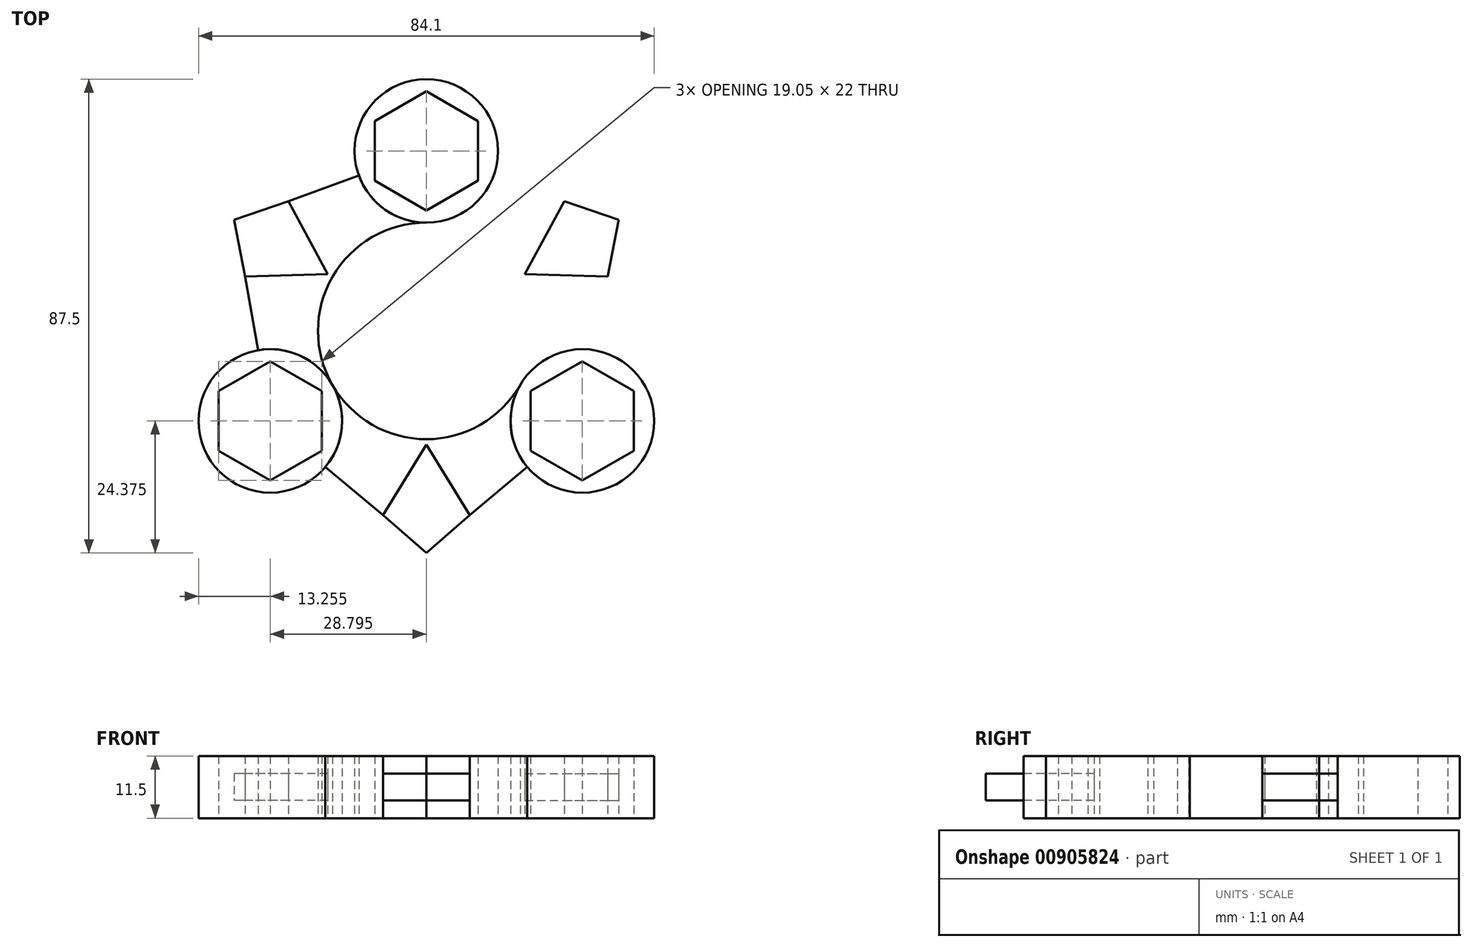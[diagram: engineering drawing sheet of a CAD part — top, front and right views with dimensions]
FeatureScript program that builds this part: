
annotation { "Feature Type Name" : "Feature", "Feature Type Description" : "" }
export const myFeature = defineFeature(function(context is Context, id is Id, definition is map)
    precondition{}
    {
        {
            var Q0;
            Q0=qCreatedBy(makeId("Top.planeOp"),FACE);
            var sketch = newSketch(context, id + "F0", { "sketchPlane" : qUnion([Q0])});
            skCircle(sketch, "E0", {"center": v(0, 0) * mm, "radius": 20 * mm});
            skLineSegment(sketch, "E1", {"start": v(0, 22.25) * mm, "end": v(0, 44.25) * mm});
            skCircle(sketch, "E2", {"center": v(0, 33.25) * mm, "radius": 11 * mm});
            skLineSegment(sketch, "E3", {"start": v(0, 44.25) * mm, "end": v(9.53, 38.75) * mm});
            skLineSegment(sketch, "E4", {"start": v(9.53, 38.75) * mm, "end": v(9.53, 27.75) * mm});
            skLineSegment(sketch, "E5", {"start": v(9.53, 27.75) * mm, "end": v(0, 22.25) * mm});
            skLineSegment(sketch, "E6", {"start": v(0, 22.25) * mm, "end": v(-9.53, 27.75) * mm});
            skLineSegment(sketch, "E7", {"start": v(-9.53, 27.75) * mm, "end": v(-9.53, 38.75) * mm});
            skLineSegment(sketch, "E8", {"start": v(-9.53, 38.75) * mm, "end": v(0, 44.25) * mm});
            skCircle(sketch, "E9", {"center": v(0, 33.25) * mm, "radius": 13.25 * mm});
            skLineSegment(sketch, "E10.1.0", {"start": v(-19.27, -22.12) * mm, "end": v(-28.8, -27.62) * mm});
            skLineSegment(sketch, "E10.1.1", {"start": v(-28.8, -27.62) * mm, "end": v(-38.32, -22.12) * mm});
            skLineSegment(sketch, "E10.1.2", {"start": v(-38.32, -22.12) * mm, "end": v(-38.32, -11.13) * mm});
            skLineSegment(sketch, "E10.1.3", {"start": v(-38.32, -11.13) * mm, "end": v(-28.8, -5.62) * mm});
            skLineSegment(sketch, "E10.1.4", {"start": v(-28.8, -5.63) * mm, "end": v(-19.27, -11.13) * mm});
            skLineSegment(sketch, "E10.1.5", {"start": v(-19.27, -11.12) * mm, "end": v(-19.27, -22.12) * mm});
            skCircle(sketch, "E10.1.6", {"center": v(-28.8, -16.62) * mm, "radius": 11 * mm});
            skCircle(sketch, "E10.1.7", {"center": v(-28.8, -16.62) * mm, "radius": 13.25 * mm});
            skLineSegment(sketch, "E10.2.0", {"start": v(28.8, -5.63) * mm, "end": v(38.32, -11.13) * mm});
            skLineSegment(sketch, "E10.2.1", {"start": v(38.32, -11.13) * mm, "end": v(38.32, -22.13) * mm});
            skLineSegment(sketch, "E10.2.2", {"start": v(38.32, -22.13) * mm, "end": v(28.8, -27.63) * mm});
            skLineSegment(sketch, "E10.2.3", {"start": v(28.8, -27.63) * mm, "end": v(19.27, -22.13) * mm});
            skLineSegment(sketch, "E10.2.4", {"start": v(19.27, -22.13) * mm, "end": v(19.27, -11.13) * mm});
            skLineSegment(sketch, "E10.2.5", {"start": v(19.27, -11.13) * mm, "end": v(28.8, -5.63) * mm});
            skCircle(sketch, "E10.2.6", {"center": v(28.8, -16.63) * mm, "radius": 11 * mm});
            skCircle(sketch, "E10.2.7", {"center": v(28.8, -16.63) * mm, "radius": 13.25 * mm});
            skLineSegment(sketch, "E11", {"start": v(0, 0) * mm, "end": v(17.32, 10) * mm});
            skLineSegment(sketch, "E12", {"start": v(17.32, 10) * mm, "end": v(35.5, 20.5) * mm});
            skLineSegment(sketch, "E13", {"start": v(35.5, 20.5) * mm, "end": v(18.19, 10.5) * mm});
            skLineSegment(sketch, "E14", {"start": v(18.19, 10.5) * mm, "end": v(33.44, 10.07) * mm});
            skLineSegment(sketch, "E15", {"start": v(33.44, 10.07) * mm, "end": v(35.5, 20.5) * mm});
            skLineSegment(sketch, "E16", {"start": v(33.44, 10.07) * mm, "end": v(29.44, 17) * mm});
            skLineSegment(sketch, "E17.MirrorCS", {"start": v(18.19, 10.5) * mm, "end": v(25.44, 23.93) * mm});
            skLineSegment(sketch, "E18.MirrorCS", {"start": v(25.44, 23.93) * mm, "end": v(35.5, 20.5) * mm});
            skLineSegment(sketch, "E19", {"start": v(0, 33.25) * mm, "end": v(25.44, 23.93) * mm});
            skLineSegment(sketch, "E20", {"start": v(33.44, 10.07) * mm, "end": v(28.8, -16.62) * mm});
            skLineSegment(sketch, "E21.1.0", {"start": v(-28.8, -16.63) * mm, "end": v(-33.44, 10.07) * mm});
            skLineSegment(sketch, "E21.1.1", {"start": v(-33.44, 10.07) * mm, "end": v(-35.5, 20.5) * mm});
            skLineSegment(sketch, "E21.1.2", {"start": v(-18.19, 10.5) * mm, "end": v(-33.44, 10.07) * mm});
            skLineSegment(sketch, "E21.1.3", {"start": v(-18.19, 10.5) * mm, "end": v(-25.44, 23.93) * mm});
            skLineSegment(sketch, "E21.1.4", {"start": v(-25.44, 23.93) * mm, "end": v(-35.5, 20.5) * mm});
            skLineSegment(sketch, "E21.1.5", {"start": v(-25.44, 23.93) * mm, "end": v(0, 33.25) * mm});
            skLineSegment(sketch, "E21.2.0", {"start": v(28.8, -16.63) * mm, "end": v(8, -34) * mm});
            skLineSegment(sketch, "E21.2.1", {"start": v(8, -34) * mm, "end": v(0, -41) * mm});
            skLineSegment(sketch, "E21.2.2", {"start": v(0, -21) * mm, "end": v(8, -34) * mm});
            skLineSegment(sketch, "E21.2.3", {"start": v(0, -21) * mm, "end": v(-8, -34) * mm});
            skLineSegment(sketch, "E21.2.4", {"start": v(-8, -34) * mm, "end": v(0, -41) * mm});
            skLineSegment(sketch, "E21.2.5", {"start": v(-8, -34) * mm, "end": v(-28.8, -16.62) * mm});
            skSolve(sketch);
        }
        {
            var Q0;
            {var subQ1=sQuery(id+"F0.wireOp",EDGE,"E12");Q0=makeQuery(id+"F0.imprint","IMPRINT",FACE,{"disambiguationData":[TD([[makeQuery(id+"F0.imprint","IMPRINT",EDGE,{"derivedFrom":subQ1}),1.0]])]});}
            var Q1;
            {var subQ6=sQuery(id+"F0.wireOp",EDGE,"E12");Q1=makeQuery(id+"F0.imprint","IMPRINT",FACE,{"disambiguationData":[TD([[makeQuery(id+"F0.imprint","IMPRINT",EDGE,{"derivedFrom":subQ6}),-1.0]])]});}
            var Q2;
            {var subQ0=sQuery(id+"F0.wireOp",EDGE,"E21.2.2");Q2=makeQuery(id+"F0.imprint","IMPRINT",FACE,{"disambiguationData":[TD([[makeQuery(id+"F0.imprint","IMPRINT",EDGE,{"derivedFrom":subQ0}),1.0]])]});}
            var Q3;
            {var subQ0=sQuery(id+"F0.wireOp",EDGE,"E21.1.2");Q3=makeQuery(id+"F0.imprint","IMPRINT",FACE,{"disambiguationData":[TD([[makeQuery(id+"F0.imprint","IMPRINT",EDGE,{"derivedFrom":subQ0}),1.0]])]});}
            extrude(context, id + "F1", {"entities" : qUnion([Q0, Q1, Q2, Q3]), "endBound" : BoundingType.SYMMETRIC, "depth" : 11.5 * mm, "offsetDistance" : 25 * mm});
        }
        {
            var Q0;
            {var subQ3=sQuery(id+"F0.wireOp",EDGE,"E17.MirrorCS");Q0=makeQuery(id+"F0.imprint","IMPRINT",FACE,{"disambiguationData":[TD([[makeQuery(id+"F0.imprint","IMPRINT",EDGE,{"derivedFrom":subQ3}),-1.0]])]});}
            var Q1;
            {var subQ0=sQuery(id+"F0.wireOp",EDGE,"E15");Q1=makeQuery(id+"F0.imprint","IMPRINT",FACE,{"disambiguationData":[TD([[makeQuery(id+"F0.imprint","IMPRINT",EDGE,{"derivedFrom":subQ0}),1.0]])]});}
            var Q2;
            {var subQ0=sQuery(id+"F0.wireOp",EDGE,"E14");Q2=makeQuery(id+"F0.imprint","IMPRINT",FACE,{"disambiguationData":[TD([[makeQuery(id+"F0.imprint","IMPRINT",EDGE,{"derivedFrom":subQ0}),1.0]])]});}
            var Q3;
            Q3=makeQuery(id+"F0.imprint","IMPRINT",FACE,{"disambiguationData":[TD([[makeQuery(id+"F0.imprint","IMPRINT",EDGE,{"derivedFrom":sQuery(id+"F0.wireOp",EDGE,"E21.1.1")}),-1.0]])]});
            var Q4;
            Q4=makeQuery(id+"F0.imprint","IMPRINT",FACE,{"disambiguationData":[TD([[makeQuery(id+"F0.imprint","IMPRINT",EDGE,{"derivedFrom":sQuery(id+"F0.wireOp",EDGE,"E21.2.1")}),-1.0]])]});
            extrude(context, id + "F2", {"entities" : qUnion([Q0, Q1, Q2, Q3, Q4]), "endBound" : BoundingType.SYMMETRIC, "depth" : 5 * mm, "offsetDistance" : 25 * mm});
        }
        {
            var Q0;
            {var subQ7=sQuery(id+"F0.wireOp",EDGE,"E20");var subQ9=sQuery(id+"F0.wireOp",EDGE,"E10.2.7");var subQ10=makeQuery(id+"F0.imprint","INTERSECT",VERTEX,{"derivedFrom":[subQ9,subQ7]});Q0=makeQuery(id+"F0.imprint","IMPRINT",FACE,{"disambiguationData":[TD([[makeQuery(id+"F0.imprint","IMPRINT",EDGE,{"disambiguationData":[TD([[subQ10,1.0]])],"derivedFrom":subQ9}),1.0]])]});}
            var Q1;
            {var subQ1=sQuery(id+"F0.wireOp",EDGE,"E10.2.0");var subQ3=sQuery(id+"F0.wireOp",EDGE,"E20");var subQ4=makeQuery(id+"F0.imprint","INTERSECT",VERTEX,{"derivedFrom":[subQ1,subQ3]});Q1=makeQuery(id+"F0.imprint","IMPRINT",FACE,{"disambiguationData":[TD([[makeQuery(id+"F0.imprint","IMPRINT",EDGE,{"disambiguationData":[TD([[subQ4,1.0]])],"derivedFrom":subQ3}),1.0]])]});}
            var Q2;
            {var subQ0=sQuery(id+"F0.wireOp",EDGE,"E10.2.1");Q2=makeQuery(id+"F0.imprint","IMPRINT",FACE,{"disambiguationData":[TD([[makeQuery(id+"F0.imprint","IMPRINT",EDGE,{"derivedFrom":subQ0}),1.0]])]});}
            var Q3;
            {var subQ0=sQuery(id+"F0.wireOp",EDGE,"E10.2.2");Q3=makeQuery(id+"F0.imprint","IMPRINT",FACE,{"disambiguationData":[TD([[makeQuery(id+"F0.imprint","IMPRINT",EDGE,{"derivedFrom":subQ0}),1.0]])]});}
            var Q4;
            {var subQ1=sQuery(id+"F0.wireOp",EDGE,"E10.2.3");var subQ3=sQuery(id+"F0.wireOp",EDGE,"E21.2.0");var subQ4=makeQuery(id+"F0.imprint","INTERSECT",VERTEX,{"derivedFrom":[subQ1,subQ3]});Q4=makeQuery(id+"F0.imprint","IMPRINT",FACE,{"disambiguationData":[TD([[makeQuery(id+"F0.imprint","IMPRINT",EDGE,{"disambiguationData":[TD([[subQ4,-1.0]])],"derivedFrom":subQ3}),1.0]])]});}
            var Q5;
            {var subQ0=sQuery(id+"F0.wireOp",EDGE,"E10.2.4");Q5=makeQuery(id+"F0.imprint","IMPRINT",FACE,{"disambiguationData":[TD([[makeQuery(id+"F0.imprint","IMPRINT",EDGE,{"derivedFrom":subQ0}),1.0]])]});}
            var Q6;
            {var subQ0=sQuery(id+"F0.wireOp",EDGE,"E10.2.5");Q6=makeQuery(id+"F0.imprint","IMPRINT",FACE,{"disambiguationData":[TD([[makeQuery(id+"F0.imprint","IMPRINT",EDGE,{"derivedFrom":subQ0}),1.0]])]});}
            var Q7;
            {var subQ1=sQuery(id+"F0.wireOp",EDGE,"E10.2.0");var subQ3=sQuery(id+"F0.wireOp",EDGE,"E20");var subQ4=makeQuery(id+"F0.imprint","INTERSECT",VERTEX,{"derivedFrom":[subQ1,subQ3]});Q7=makeQuery(id+"F0.imprint","IMPRINT",FACE,{"disambiguationData":[TD([[makeQuery(id+"F0.imprint","IMPRINT",EDGE,{"disambiguationData":[TD([[subQ4,1.0]])],"derivedFrom":subQ3}),-1.0]])]});}
            var Q8;
            {var subQ8=sQuery(id+"F0.wireOp",EDGE,"E20");var subQ10=sQuery(id+"F0.wireOp",EDGE,"E10.2.7");var subQ11=makeQuery(id+"F0.imprint","INTERSECT",VERTEX,{"derivedFrom":[subQ10,subQ8]});Q8=makeQuery(id+"F0.imprint","IMPRINT",FACE,{"disambiguationData":[TD([[makeQuery(id+"F0.imprint","IMPRINT",EDGE,{"disambiguationData":[TD([[subQ11,-1.0]])],"derivedFrom":subQ10}),1.0]])]});}
            var Q9;
            {var subQ1=sQuery(id+"F0.wireOp",EDGE,"E10.2.3");var subQ3=sQuery(id+"F0.wireOp",EDGE,"E21.2.0");var subQ4=makeQuery(id+"F0.imprint","INTERSECT",VERTEX,{"derivedFrom":[subQ1,subQ3]});Q9=makeQuery(id+"F0.imprint","IMPRINT",FACE,{"disambiguationData":[TD([[makeQuery(id+"F0.imprint","IMPRINT",EDGE,{"disambiguationData":[TD([[subQ4,-1.0]])],"derivedFrom":subQ3}),-1.0]])]});}
            var Q10;
            {var subQ0=sQuery(id+"F0.wireOp",EDGE,"E10.1.5");Q10=makeQuery(id+"F0.imprint","IMPRINT",FACE,{"disambiguationData":[TD([[makeQuery(id+"F0.imprint","IMPRINT",EDGE,{"derivedFrom":subQ0}),1.0]])]});}
            var Q11;
            {var subQ8=sQuery(id+"F0.wireOp",EDGE,"E10.1.7");var subQ10=sQuery(id+"F0.wireOp",EDGE,"E21.2.5");var subQ12=makeQuery(id+"F0.imprint","INTERSECT",VERTEX,{"derivedFrom":[subQ8,subQ10]});Q11=makeQuery(id+"F0.imprint","IMPRINT",FACE,{"disambiguationData":[TD([[makeQuery(id+"F0.imprint","IMPRINT",EDGE,{"disambiguationData":[TD([[subQ12,-1.0]])],"derivedFrom":subQ8}),1.0]])]});}
            var Q12;
            {var subQ1=sQuery(id+"F0.wireOp",EDGE,"E10.1.0");var subQ3=sQuery(id+"F0.wireOp",EDGE,"E21.2.5");var subQ4=makeQuery(id+"F0.imprint","INTERSECT",VERTEX,{"derivedFrom":[subQ1,subQ3]});Q12=makeQuery(id+"F0.imprint","IMPRINT",FACE,{"disambiguationData":[TD([[makeQuery(id+"F0.imprint","IMPRINT",EDGE,{"disambiguationData":[TD([[subQ4,1.0]])],"derivedFrom":subQ3}),-1.0]])]});}
            var Q13;
            {var subQ7=sQuery(id+"F0.wireOp",EDGE,"E21.2.5");var subQ10=sQuery(id+"F0.wireOp",EDGE,"E10.1.7");var subQ11=makeQuery(id+"F0.imprint","INTERSECT",VERTEX,{"derivedFrom":[subQ10,subQ7]});Q13=makeQuery(id+"F0.imprint","IMPRINT",FACE,{"disambiguationData":[TD([[makeQuery(id+"F0.imprint","IMPRINT",EDGE,{"disambiguationData":[TD([[subQ11,1.0]])],"derivedFrom":subQ10}),1.0]])]});}
            var Q14;
            {var subQ1=sQuery(id+"F0.wireOp",EDGE,"E10.1.0");var subQ3=sQuery(id+"F0.wireOp",EDGE,"E21.2.5");var subQ4=makeQuery(id+"F0.imprint","INTERSECT",VERTEX,{"derivedFrom":[subQ1,subQ3]});Q14=makeQuery(id+"F0.imprint","IMPRINT",FACE,{"disambiguationData":[TD([[makeQuery(id+"F0.imprint","IMPRINT",EDGE,{"disambiguationData":[TD([[subQ4,1.0]])],"derivedFrom":subQ3}),1.0]])]});}
            var Q15;
            {var subQ0=sQuery(id+"F0.wireOp",EDGE,"E10.1.1");Q15=makeQuery(id+"F0.imprint","IMPRINT",FACE,{"disambiguationData":[TD([[makeQuery(id+"F0.imprint","IMPRINT",EDGE,{"derivedFrom":subQ0}),1.0]])]});}
            var Q16;
            {var subQ0=sQuery(id+"F0.wireOp",EDGE,"E10.1.2");Q16=makeQuery(id+"F0.imprint","IMPRINT",FACE,{"disambiguationData":[TD([[makeQuery(id+"F0.imprint","IMPRINT",EDGE,{"derivedFrom":subQ0}),1.0]])]});}
            var Q17;
            {var subQ1=sQuery(id+"F0.wireOp",EDGE,"E10.1.3");var subQ3=sQuery(id+"F0.wireOp",EDGE,"E21.1.0");var subQ4=makeQuery(id+"F0.imprint","INTERSECT",VERTEX,{"derivedFrom":[subQ1,subQ3]});Q17=makeQuery(id+"F0.imprint","IMPRINT",FACE,{"disambiguationData":[TD([[makeQuery(id+"F0.imprint","IMPRINT",EDGE,{"disambiguationData":[TD([[subQ4,-1.0]])],"derivedFrom":subQ3}),1.0]])]});}
            var Q18;
            {var subQ1=sQuery(id+"F0.wireOp",EDGE,"E10.1.3");var subQ3=sQuery(id+"F0.wireOp",EDGE,"E21.1.0");var subQ4=makeQuery(id+"F0.imprint","INTERSECT",VERTEX,{"derivedFrom":[subQ1,subQ3]});Q18=makeQuery(id+"F0.imprint","IMPRINT",FACE,{"disambiguationData":[TD([[makeQuery(id+"F0.imprint","IMPRINT",EDGE,{"disambiguationData":[TD([[subQ4,-1.0]])],"derivedFrom":subQ3}),-1.0]])]});}
            var Q19;
            {var subQ0=sQuery(id+"F0.wireOp",EDGE,"E10.1.4");Q19=makeQuery(id+"F0.imprint","IMPRINT",FACE,{"disambiguationData":[TD([[makeQuery(id+"F0.imprint","IMPRINT",EDGE,{"derivedFrom":subQ0}),1.0]])]});}
            var Q20;
            {var subQ1=sQuery(id+"F0.wireOp",EDGE,"E2");var subQ3=sQuery(id+"F0.wireOp",EDGE,"E21.1.5");var subQ4=makeQuery(id+"F0.imprint","INTERSECT",VERTEX,{"derivedFrom":[subQ1,subQ3]});Q20=makeQuery(id+"F0.imprint","IMPRINT",FACE,{"disambiguationData":[TD([[makeQuery(id+"F0.imprint","IMPRINT",EDGE,{"disambiguationData":[TD([[subQ4,-1.0]])],"derivedFrom":subQ3}),1.0]])]});}
            var Q21;
            {var subQ0=sQuery(id+"F0.wireOp",EDGE,"E8");Q21=makeQuery(id+"F0.imprint","IMPRINT",FACE,{"disambiguationData":[TD([[makeQuery(id+"F0.imprint","IMPRINT",EDGE,{"derivedFrom":subQ0}),1.0]])]});}
            var Q22;
            {var subQ1=sQuery(id+"F0.wireOp",EDGE,"E2");var subQ3=sQuery(id+"F0.wireOp",EDGE,"E21.1.5");var subQ4=makeQuery(id+"F0.imprint","INTERSECT",VERTEX,{"derivedFrom":[subQ1,subQ3]});Q22=makeQuery(id+"F0.imprint","IMPRINT",FACE,{"disambiguationData":[TD([[makeQuery(id+"F0.imprint","IMPRINT",EDGE,{"disambiguationData":[TD([[subQ4,-1.0]])],"derivedFrom":subQ3}),-1.0]])]});}
            var Q23;
            {var subQ0=sQuery(id+"F0.wireOp",EDGE,"E6");Q23=makeQuery(id+"F0.imprint","IMPRINT",FACE,{"disambiguationData":[TD([[makeQuery(id+"F0.imprint","IMPRINT",EDGE,{"derivedFrom":subQ0}),1.0]])]});}
            var Q24;
            {var subQ5=sQuery(id+"F0.wireOp",EDGE,"E9");var subQ10=sQuery(id+"F0.wireOp",EDGE,"E21.1.5");var subQ11=makeQuery(id+"F0.imprint","INTERSECT",VERTEX,{"derivedFrom":[subQ5,subQ10]});Q24=makeQuery(id+"F0.imprint","IMPRINT",FACE,{"disambiguationData":[TD([[makeQuery(id+"F0.imprint","IMPRINT",EDGE,{"disambiguationData":[TD([[subQ11,-1.0]])],"derivedFrom":subQ5}),1.0]])]});}
            var Q25;
            {var subQ0=sQuery(id+"F0.wireOp",EDGE,"E5");Q25=makeQuery(id+"F0.imprint","IMPRINT",FACE,{"disambiguationData":[TD([[makeQuery(id+"F0.imprint","IMPRINT",EDGE,{"derivedFrom":subQ0}),1.0]])]});}
            var Q26;
            {var subQ1=sQuery(id+"F0.wireOp",EDGE,"E2");var subQ3=sQuery(id+"F0.wireOp",EDGE,"E19");var subQ4=makeQuery(id+"F0.imprint","INTERSECT",VERTEX,{"derivedFrom":[subQ1,subQ3]});Q26=makeQuery(id+"F0.imprint","IMPRINT",FACE,{"disambiguationData":[TD([[makeQuery(id+"F0.imprint","IMPRINT",EDGE,{"disambiguationData":[TD([[subQ4,1.0]])],"derivedFrom":subQ3}),1.0]])]});}
            var Q27;
            {var subQ5=sQuery(id+"F0.wireOp",EDGE,"E21.1.5");var subQ6=sQuery(id+"F0.wireOp",EDGE,"E9");var subQ7=makeQuery(id+"F0.imprint","INTERSECT",VERTEX,{"derivedFrom":[subQ6,subQ5]});Q27=makeQuery(id+"F0.imprint","IMPRINT",FACE,{"disambiguationData":[TD([[makeQuery(id+"F0.imprint","IMPRINT",EDGE,{"disambiguationData":[TD([[subQ7,1.0]])],"derivedFrom":subQ6}),1.0]])]});}
            var Q28;
            {var subQ0=sQuery(id+"F0.wireOp",EDGE,"E3");Q28=makeQuery(id+"F0.imprint","IMPRINT",FACE,{"disambiguationData":[TD([[makeQuery(id+"F0.imprint","IMPRINT",EDGE,{"derivedFrom":subQ0}),1.0]])]});}
            var Q29;
            {var subQ1=sQuery(id+"F0.wireOp",EDGE,"E2");var subQ3=sQuery(id+"F0.wireOp",EDGE,"E19");var subQ4=makeQuery(id+"F0.imprint","INTERSECT",VERTEX,{"derivedFrom":[subQ1,subQ3]});Q29=makeQuery(id+"F0.imprint","IMPRINT",FACE,{"disambiguationData":[TD([[makeQuery(id+"F0.imprint","IMPRINT",EDGE,{"disambiguationData":[TD([[subQ4,1.0]])],"derivedFrom":subQ3}),-1.0]])]});}
            extrude(context, id + "F3", {"entities" : qUnion([Q0, Q1, Q2, Q3, Q4, Q5, Q6, Q7, Q8, Q9, Q10, Q11, Q12, Q13, Q14, Q15, Q16, Q17, Q18, Q19, Q20, Q21, Q22, Q23, Q24, Q25, Q26, Q27, Q28, Q29]), "endBound" : BoundingType.SYMMETRIC, "depth" : 11.5 * mm, "offsetDistance" : 25 * mm});
        }
    });
